# Revit family: Urinal_Washdown-Top_Spud-Sloan-(SU-1006_SU-1009)_Series
name_source: partatom
category: Plumbing Fixtures
revit_build: Autodesk Revit 2014 (Build: 20130308_1515(x64)
units: mm (PartAtom-declared; Revit-internal decimal feet)

## types (3) — shared parameters
ADA Compliant = Yes
Assembly Code = D2010210
Buy American Act Compliant = Yes
CW Connection = Yes
CWFU = 5
Cold Water Connection Diameter = 3/4"
Cold Water Connection Height = 32 3/4"
Cold Water Connection Radius = 3/8"
Default Elevation = 17"
Fixture Color = White
Flush Choice = Single Flush
HW Connection = No
Height = 32 3/4"
High Efficiency = Yes
IAPMO Compliance = cUPC
Length = 14 1/4"
Manufacturer = SLOAN
Material = Porcelain-Sloan-White
Mounting = Wall Hung
Price = Prices may vary. Please consult Sloan Rep for most up-to-date price list.
Product Documentation Link = https://specifications.sloan.com
Product Page URL = https://www.sloan.com
Revision Date = "8/10/2015"
Spud Location = Top Spud
URL = www.sloan.com
Vent Connection = No
WFU = 5
Warranty = 3 Year (Limited)
Waste Connection = Yes
Waste Connection Diameter = 2"
Waste Connection Radius = 1"
Width = 15 5/8"
zero-valued in all types: HWFU

## per-type parameters (varying)
| type | Description | Flush Volume | Inlet Spud Diameter | Model | Order Code | Waste Outlet Diameter |
| SU-1009 | Standard Top Spud Urinal - 0.125 to 0.5 gpf (0.5 to 1.9 Lpf) | 0.125 gpf (0.5 Lpf)/0.5 gpf (1.9 Lpf) | 3/4" | SU-1009 | 1101009 | 2" |
| SU-1009-STG | Standard HE Top Spud Urinal w/ SloanTec Glaze | 0.125 gpf (0.5 Lpf)/0.5 gpf (1.9 Lpf) | 3/8" | SU-1009-STG | 1171009 | 1" |
| SU-1006 | Standard Top Spud Urinal - 1.0 gpf (3.8 Lpf) | 1.0 gpf / 3.8 lpf | 3/4" | SU-1009 | 1101006 | 2" |

## geometry (parser evidence)
native form markers: Sweep x1
no freeform markers — native parametric forms only
